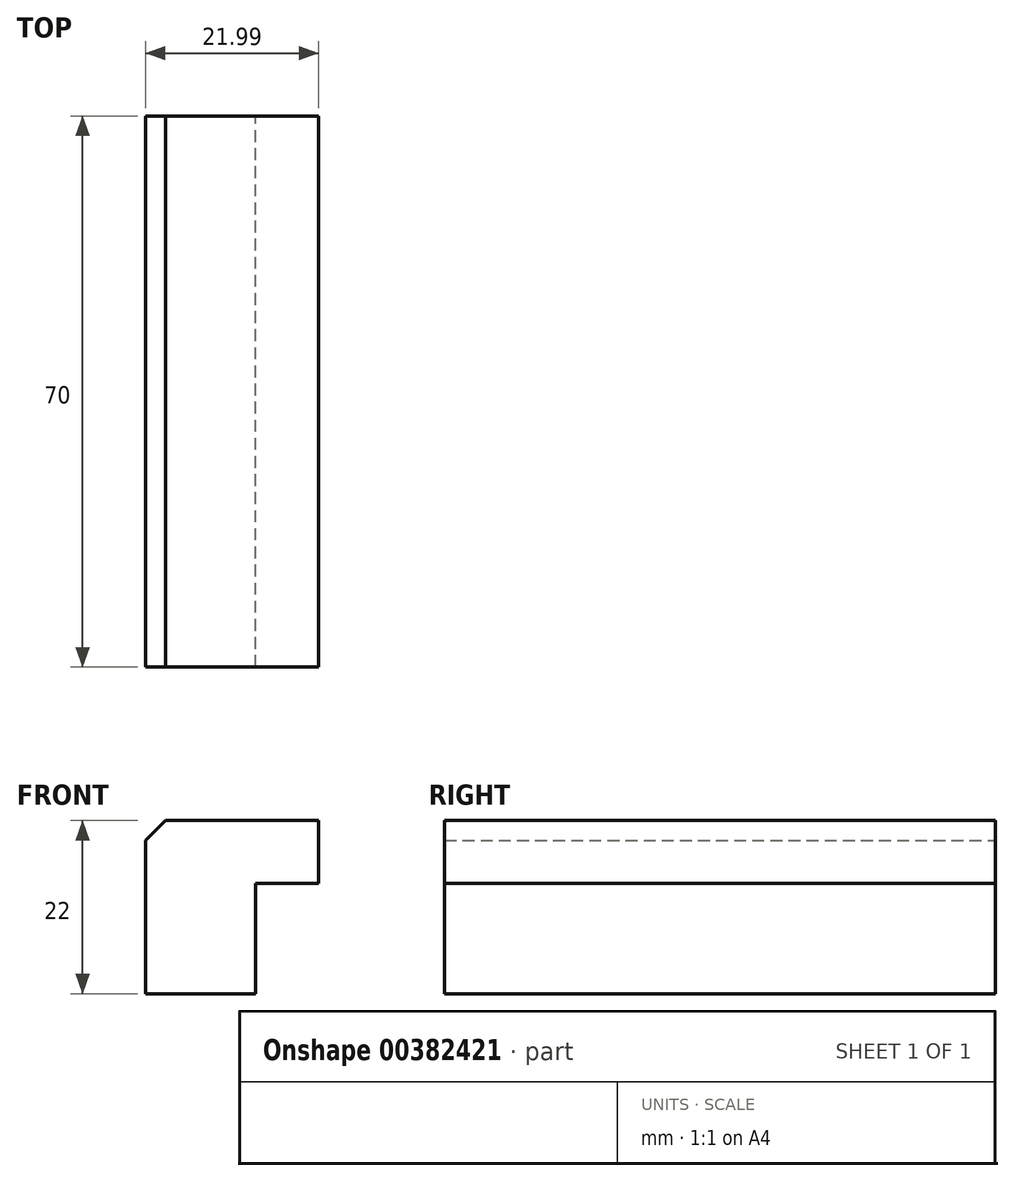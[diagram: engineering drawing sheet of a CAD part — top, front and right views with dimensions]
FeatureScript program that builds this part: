
annotation { "Feature Type Name" : "Feature", "Feature Type Description" : "" }
export const myFeature = defineFeature(function(context is Context, id is Id, definition is map)
    precondition{}
    {
        {
            var Q0;
            Q0=qCreatedBy(makeId("Front.planeOp"),FACE);
            var sketch = newSketch(context, id + "F0", { "sketchPlane" : qUnion([Q0])});
            skLineSegment(sketch, "E0", {"start": v(-19.73, 22) * mm, "end": v(-19.73, 0) * mm});
            skLineSegment(sketch, "E1", {"start": v(-19.73, 0) * mm, "end": v(-5.74, 0) * mm});
            skLineSegment(sketch, "E2", {"start": v(-5.74, 0) * mm, "end": v(-5.74, 14) * mm});
            skLineSegment(sketch, "E3", {"start": v(-5.74, 14) * mm, "end": v(2.26, 14) * mm});
            skLineSegment(sketch, "E4", {"start": v(2.26, 14) * mm, "end": v(2.26, 22) * mm});
            skLineSegment(sketch, "E5", {"start": v(2.26, 22) * mm, "end": v(-19.73, 22) * mm});
            skSolve(sketch);
        }
        {
            var Q0;
            Q0 = qSketchRegion(id + "F0", true);
            extrude(context, id + "F1", {"entities" : qUnion([Q0]), "depth" : 70 * mm});
        }
        {
            var Q0;
            Q0=makeQuery(id+"F1.opExtrude","SWEPT_EDGE",EDGE,{"disambiguationData":[OSD([sQuery(id+"F0.wireOp",EDGE,"E0"),sQuery(id+"F0.wireOp",EDGE,"E5")])]});
            chamfer(context, id + "F2", {"entities" : qUnion([Q0]), "width" : 2.54 * mm, "tangentPropagation" : true});
        }
    });
